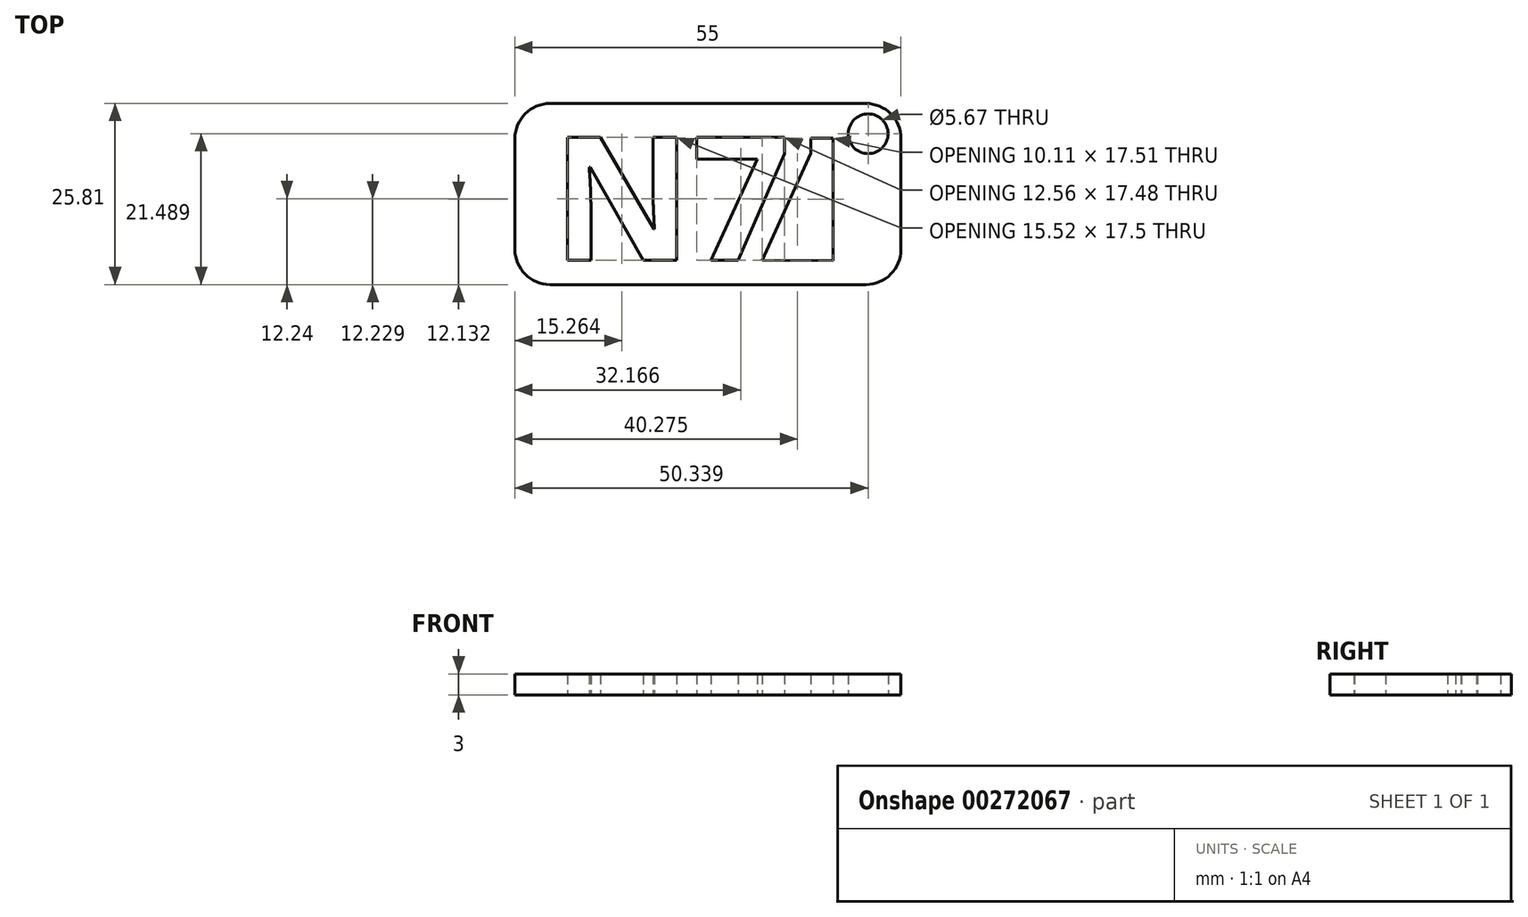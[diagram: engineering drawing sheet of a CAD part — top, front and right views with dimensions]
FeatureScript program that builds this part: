
annotation { "Feature Type Name" : "Feature", "Feature Type Description" : "" }
export const myFeature = defineFeature(function(context is Context, id is Id, definition is map)
    precondition{}
    {
        {
            var Q0;
            Q0=qCreatedBy(makeId("Top.planeOp"),FACE);
            var sketch = newSketch(context, id + "F0", { "sketchPlane" : qUnion([Q0])});
            skLineSegment(sketch, "E0.bottom", {"start": v(15.78, 7.12) * mm, "end": v(-39.22, 7.12) * mm});
            skLineSegment(sketch, "E0.top", {"start": v(15.78, -18.7) * mm, "end": v(-39.22, -18.7) * mm});
            skLineSegment(sketch, "E0.left", {"start": v(15.78, 7.12) * mm, "end": v(15.78, -18.7) * mm});
            skLineSegment(sketch, "E0.right", {"start": v(-39.22, 7.12) * mm, "end": v(-39.22, -18.7) * mm});
            skCircle(sketch, "E1", {"center": v(11.12, 2.8) * mm, "radius": 2.84 * mm});
            skText(sketch, "E2", { "text": "N7", "fontName": "OpenSans-Bold.ttf"});
            skLineSegment(sketch, "E3", {"start": v(-4, -15.2) * mm, "end": v(2.92, 0) * mm});
            skLineSegment(sketch, "E4", {"start": v(2.92, 0) * mm, "end": v(2.92, 2.2) * mm});
            skLineSegment(sketch, "E5", {"start": v(2.92, 2.2) * mm, "end": v(6.11, 2.2) * mm});
            skLineSegment(sketch, "E6", {"start": v(6.11, 2.2) * mm, "end": v(6.11, -15.31) * mm});
            skLineSegment(sketch, "E7", {"start": v(6.11, -15.31) * mm, "end": v(-4, -15.2) * mm});
            const initialGuessF0  = {"E2": [-0.03392, -0.0152, 1, 0, 0.01765]};
            skSetInitialGuess(sketch, initialGuessF0);
            skSolve(sketch);
        }
        {
            var Q0;
            Q0 = qSketchRegion(id + "F0", true);
            extrude(context, id + "F1", {"entities" : qUnion([Q0]), "depth" : 3 * mm});
        }
        {
            var Q0;
            Q0=makeQuery(id+"F1.opExtrude","SWEPT_EDGE",EDGE,{"disambiguationData":[OSD([sQuery(id+"F0.wireOp",EDGE,"E0.bottom"),sQuery(id+"F0.wireOp",EDGE,"E0.right")])]});
            var Q1;
            Q1=makeQuery(id+"F1.opExtrude","SWEPT_EDGE",EDGE,{"disambiguationData":[OSD([sQuery(id+"F0.wireOp",EDGE,"E0.top"),sQuery(id+"F0.wireOp",EDGE,"E0.right")])]});
            var Q2;
            Q2=makeQuery(id+"F1.opExtrude","SWEPT_EDGE",EDGE,{"disambiguationData":[OSD([sQuery(id+"F0.wireOp",EDGE,"E0.bottom"),sQuery(id+"F0.wireOp",EDGE,"E0.left")])]});
            var Q3;
            Q3=makeQuery(id+"F1.opExtrude","SWEPT_EDGE",EDGE,{"disambiguationData":[OSD([sQuery(id+"F0.wireOp",EDGE,"E0.top"),sQuery(id+"F0.wireOp",EDGE,"E0.left")])]});
            fillet(context, id + "F2", {"entities" : qUnion([Q0, Q1, Q2, Q3]), "radius" : 5 * mm, "tangentPropagation" : true, "allowEdgeOverflow" : false});
        }
    });
